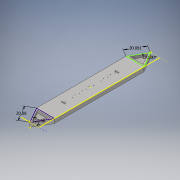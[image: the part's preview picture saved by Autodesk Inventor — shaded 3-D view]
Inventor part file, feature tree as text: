
AUTODESK INVENTOR PART (.ipt)
format: ipt  version: 2016 (Build 200138000, 138)  size: 216,576 bytes
history: native  units: in
note: dims shown in document units (in); Inventor stores cm internally (conversion verified against a paired STEP export)
features: sketch x15, extrude x12, other x4, plane x4, split x4
ambient origin geometry x8: Origin, YZ Plane, XZ Plane, XY Plane, X Axis, Y Axis, Z Axis, Center Point
bodies: Solid1 (feature_tree)
feature tree (39):
  extrude  "Extrusion1"  Depth=7.9055in
  other  "Work Point1"
  other  "Work Point2"
  sketch  "Sketch2"  dims[d2=2.0in d3=0.0in d4=7.9055in]
  plane  "Work Plane1"
  split  "Split1"
  plane  "Work Plane2"
  other  "Work Point3"
  other  "Work Point4"
  plane  "Work Plane3"
  split  "Split2"
  split  "Split3"
  plane  "Work Plane4"
  split  "Split4"
  sketch  "Sketch3"  dims[d5=120.0deg d6=7.906in]
  sketch  "Sketch4"  dims[d7=120.0deg d8=5.9055in]
  sketch  "Sketch5"  dims[d9=5.9055in d10=5.9055in]
  extrude  "Extrusion2"  Depth=7.9055in
  extrude  "Extrusion3"  Depth=7.906in
  extrude  "Extrusion6"  Depth=5.9055in
  extrude  "Extrusion7"  Depth=5.9055in
  extrude  "Extrusion8"  TaperAngle=60.0deg  [1 undecoded]
  extrude  "Extrusion9"  Depth=5.9055in
  extrude  "Extrusion10"  Depth=1.0in TaperAngle=0.0deg
  extrude  "Extrusion11"  Depth=0.3937in
  extrude  "Extrusion12"  Depth=1.5748in
  extrude  "Extrusion13"  Depth=2.0in TaperAngle=0.0deg
  extrude  "Extrusion14"  Depth=0.1969in
  sketch  "Sketch1"  dims[d0=7.9055in d1=53.4206in]
  sketch  "Sketch6"  dims[d11=5.9055in d12=60.0deg]
  sketch  "Sketch11"  dims[d13=1.0in d14=0.0in d15=5.9055in]
  sketch  "Sketch12"  dims[d16=5.9055in d17=1.0in d18=0.0in]
  sketch  "Sketch13"  dims[d42=1.5748in d43=0.3937in]
  sketch  "Sketch14"  dims[d44=2.0in d45=0.0in d46=1.5748in]
  sketch  "Sketch15"  dims[d47=0.3937in d48=2.0in d49=0.0in]
  sketch  "Sketch16"  dims[d50=0.1969in d51=0.1969in]
  sketch  "Sketch17"  dims[d52=0.1969in]
  sketch  "Sketch18"  dims[d53=0.1969in]
  sketch  "Sketch19"  dims[d54=0.1969in d55=0.1969in d56=0.1969in d57=2.0in d58=0.0in d59=0.1969in d60=2.0in d61=0.0in d62=0.1969in d63=2.0in d64=0.0in d65=0.1969in d66=0.1969in d67=2.0in d68=0.0in d69=0.1969in d70=0.1969in d71=0.1969in d72=2.0in d73=0.0in d74=0.1969in d75=0.1969in d76=0.1969in d77=0.1969in d78=0.1969in d79=2.0in d80=0.0in d81=1.0in d82=0.0in]
note: 1 required parameter value undecoded (feature->parameter linkage not recoverable at this tier; creation-order binding heuristic only, values carry confidence <= 0.55)
